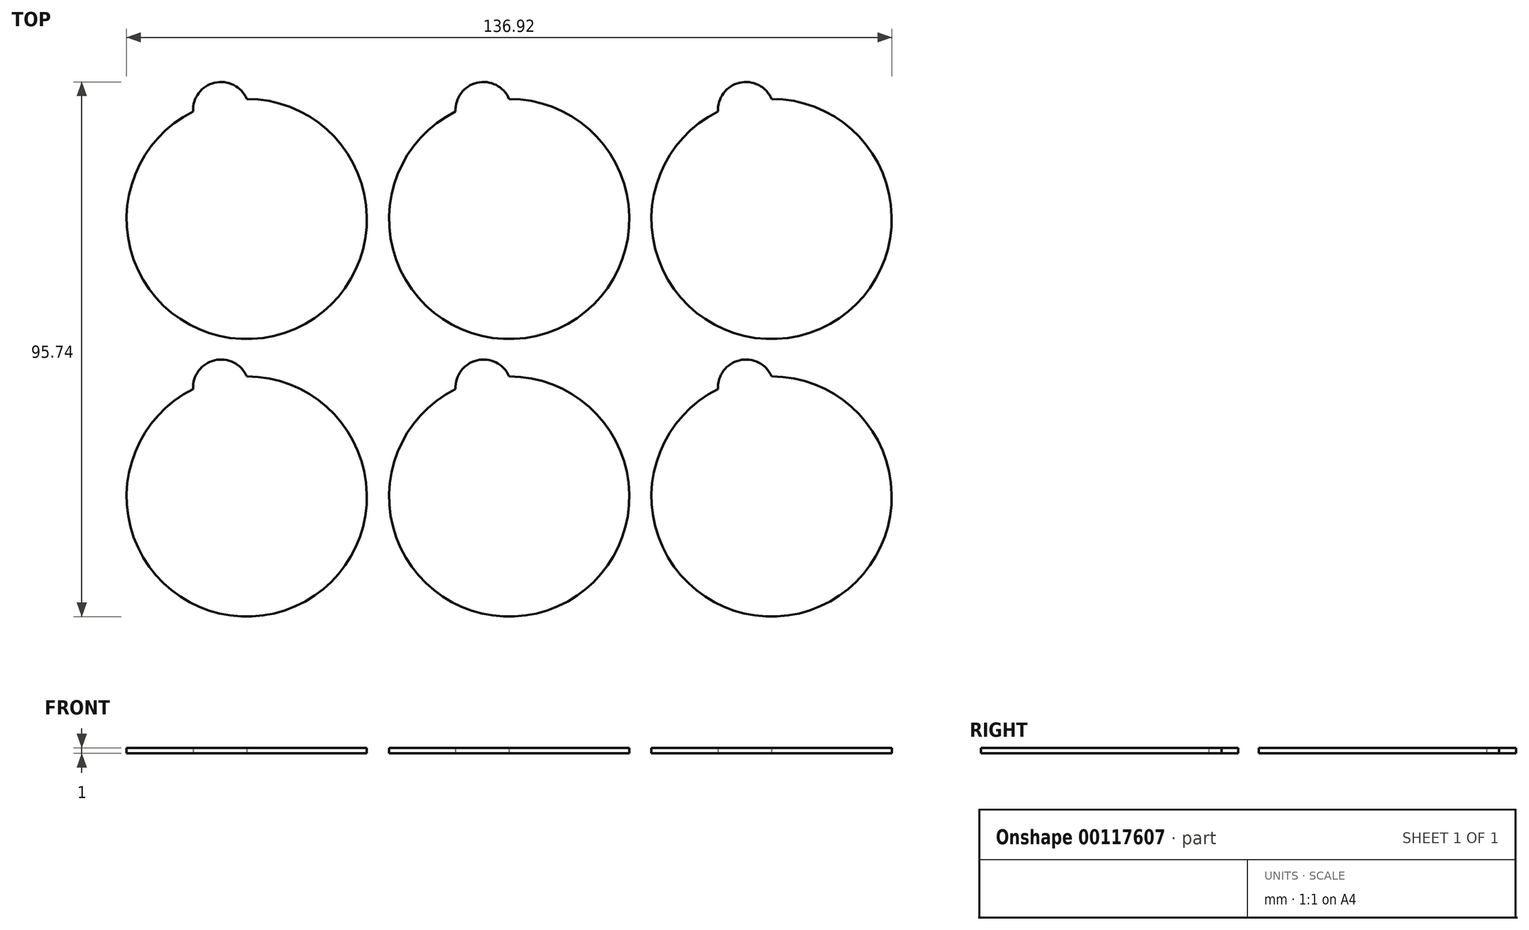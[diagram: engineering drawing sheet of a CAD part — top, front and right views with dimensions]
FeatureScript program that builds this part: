
annotation { "Feature Type Name" : "Feature", "Feature Type Description" : "" }
export const myFeature = defineFeature(function(context is Context, id is Id, definition is map)
    precondition{}
    {
        {
            var Q0;
            Q0=qCreatedBy(makeId("Top.planeOp"),FACE);
            var sketch = newSketch(context, id + "F0", { "sketchPlane" : qUnion([Q0])});
            skArc(sketch, "E0", {"start": v(-9.59, 19.24) * mm, "mid": v(4.92, -20.93) * mm, "end": v(0, 21.5) * mm});
            skArc(sketch, "E1", {"start": v(0, 21.5) * mm, "mid": v(-5.74, 24.4) * mm, "end": v(-9.59, 19.24) * mm});
            skArc(sketch, "E2.0.1.0", {"start": v(-9.59, 68.95) * mm, "mid": v(4.92, 28.78) * mm, "end": v(0, 71.2) * mm});
            skArc(sketch, "E2.0.1.1", {"start": v(0, 71.2) * mm, "mid": v(-5.74, 74.1) * mm, "end": v(-9.59, 68.95) * mm});
            skArc(sketch, "E2.1.0.0", {"start": v(37.37, 19.24) * mm, "mid": v(51.89, -20.93) * mm, "end": v(46.96, 21.5) * mm});
            skArc(sketch, "E2.1.0.1", {"start": v(46.96, 21.5) * mm, "mid": v(41.22, 24.4) * mm, "end": v(37.37, 19.24) * mm});
            skArc(sketch, "E2.1.1.0", {"start": v(37.37, 68.95) * mm, "mid": v(51.89, 28.78) * mm, "end": v(46.96, 71.2) * mm});
            skArc(sketch, "E2.1.1.1", {"start": v(46.96, 71.2) * mm, "mid": v(41.22, 74.1) * mm, "end": v(37.37, 68.95) * mm});
            skArc(sketch, "E2.2.0.0", {"start": v(84.33, 19.24) * mm, "mid": v(98.85, -20.93) * mm, "end": v(93.92, 21.5) * mm});
            skArc(sketch, "E2.2.0.1", {"start": v(93.92, 21.5) * mm, "mid": v(88.18, 24.4) * mm, "end": v(84.33, 19.24) * mm});
            skArc(sketch, "E2.2.1.0", {"start": v(84.33, 68.95) * mm, "mid": v(98.85, 28.78) * mm, "end": v(93.92, 71.2) * mm});
            skArc(sketch, "E2.2.1.1", {"start": v(93.92, 71.2) * mm, "mid": v(88.18, 74.1) * mm, "end": v(84.33, 68.95) * mm});
            skLineSegment(sketch, "E2.direction1", {"start": v(0, 0) * mm, "end": v(46.96, 0) * mm, "construction": true});
            skLineSegment(sketch, "E2.direction2", {"start": v(0, 0) * mm, "end": v(0, 49.7) * mm, "construction": true});
            skSolve(sketch);
        }
        {
            var Q0;
            Q0=makeQuery(id+"F0.imprint","IMPRINT",FACE,{"disambiguationData":[TD([[makeQuery(id+"F0.imprint","IMPRINT",EDGE,{"derivedFrom":sQuery(id+"F0.wireOp",EDGE,"E0")}),1.0]])]});
            var Q1;
            Q1=makeQuery(id+"F0.imprint","IMPRINT",FACE,{"disambiguationData":[TD([[makeQuery(id+"F0.imprint","IMPRINT",EDGE,{"derivedFrom":sQuery(id+"F0.wireOp",EDGE,"E2.0.1.0")}),1.0]])]});
            var Q2;
            Q2=makeQuery(id+"F0.imprint","IMPRINT",FACE,{"disambiguationData":[TD([[makeQuery(id+"F0.imprint","IMPRINT",EDGE,{"derivedFrom":sQuery(id+"F0.wireOp",EDGE,"E2.1.1.0")}),1.0]])]});
            var Q3;
            Q3=makeQuery(id+"F0.imprint","IMPRINT",FACE,{"disambiguationData":[TD([[makeQuery(id+"F0.imprint","IMPRINT",EDGE,{"derivedFrom":sQuery(id+"F0.wireOp",EDGE,"E2.2.1.0")}),1.0]])]});
            var Q4;
            Q4=makeQuery(id+"F0.imprint","IMPRINT",FACE,{"disambiguationData":[TD([[makeQuery(id+"F0.imprint","IMPRINT",EDGE,{"derivedFrom":sQuery(id+"F0.wireOp",EDGE,"E2.1.0.0")}),1.0]])]});
            var Q5;
            Q5=makeQuery(id+"F0.imprint","IMPRINT",FACE,{"disambiguationData":[TD([[makeQuery(id+"F0.imprint","IMPRINT",EDGE,{"derivedFrom":sQuery(id+"F0.wireOp",EDGE,"E2.2.0.0")}),1.0]])]});
            extrude(context, id + "F1", {"entities" : qUnion([Q0, Q1, Q2, Q3, Q4, Q5]), "depth" : 1 * mm});
        }
    });
